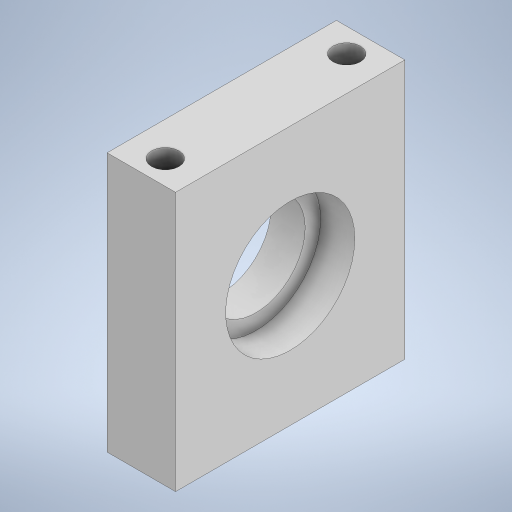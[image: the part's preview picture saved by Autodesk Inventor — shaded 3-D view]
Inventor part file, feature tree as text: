
AUTODESK INVENTOR PART (.ipt)
format: ipt  version: 2023 (Build 270158000, 158)  size: 235,008 bytes
history: native  units: mm
features: sketch x4, extrude x3, other x1, hole x1
ambient origin geometry x8: Origin, YZ Plane, XZ Plane, XY Plane, X Axis, Y Axis, Z Axis, Center Point
bodies: Body1 (feature_tree)
feature tree (9):
  other  "Твердое тело1"
  extrude  "Выдавливание1"  Depth=30.3mm
  hole  "Отверстие1"  [1 undecoded]
  extrude  "Выдавливание2"  Depth=8.0mm TaperAngle=0.0deg
  extrude  "Выдавливание3"  Depth=21.2mm
  sketch  "Эскиз1"
  sketch  "Эскиз2"
  sketch  "Эскиз3"
  sketch  "Эскиз4"
note: 1 required parameter value undecoded (feature->parameter linkage not recoverable at this tier; creation-order binding heuristic only, values carry confidence <= 0.55)
